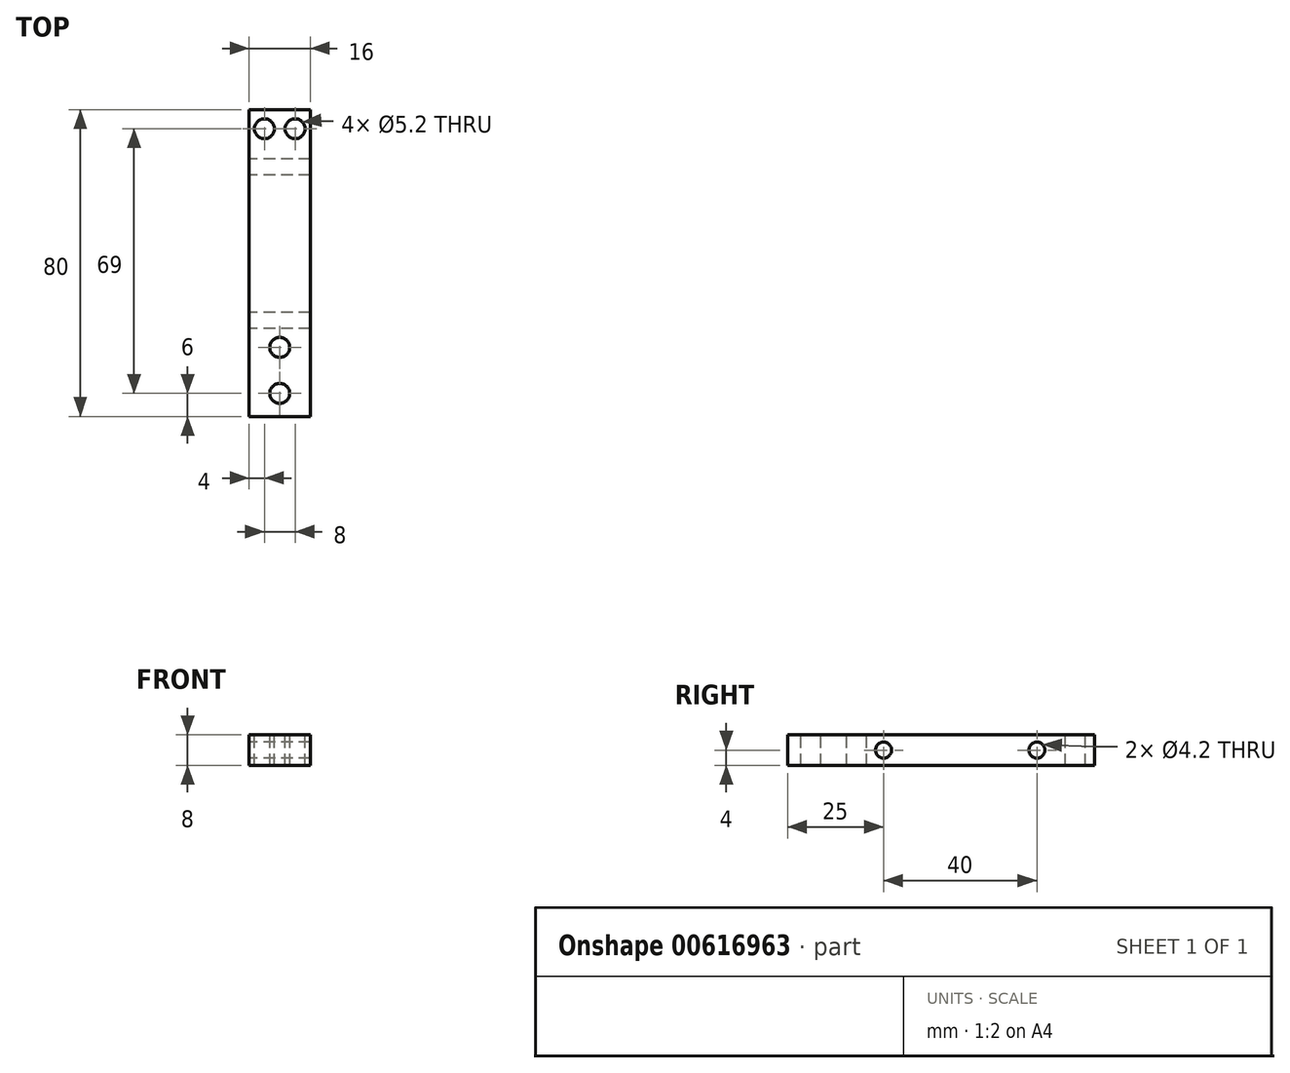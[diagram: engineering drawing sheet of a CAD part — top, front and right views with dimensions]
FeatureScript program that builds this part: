
annotation { "Feature Type Name" : "Feature", "Feature Type Description" : "" }
export const myFeature = defineFeature(function(context is Context, id is Id, definition is map)
    precondition{}
    {
        {
            var Q0;
            Q0=qCreatedBy(makeId("Front.planeOp"),FACE);
            var sketch = newSketch(context, id + "F0", { "sketchPlane" : qUnion([Q0])});
            skLineSegment(sketch, "E0.bottom", {"start": v(-8, 4) * mm, "end": v(8, 4) * mm});
            skLineSegment(sketch, "E0.top", {"start": v(-8, -4) * mm, "end": v(8, -4) * mm});
            skLineSegment(sketch, "E0.left", {"start": v(-8, 4) * mm, "end": v(-8, -4) * mm});
            skLineSegment(sketch, "E0.right", {"start": v(8, 4) * mm, "end": v(8, -4) * mm});
            skSolve(sketch);
        }
        {
            var Q0;
            Q0=makeQuery(id+"F0.imprint","IMPRINT",FACE,{"disambiguationData":[TD([[makeQuery(id+"F0.imprint","IMPRINT",EDGE,{"derivedFrom":sQuery(id+"F0.wireOp",EDGE,"E0.bottom")}),-1.0]])]});
            extrude(context, id + "F1", {"entities" : qUnion([Q0]), "oppositeDirection" : true, "depth" : 80 * mm, "offsetDistance" : 25 * mm});
        }
        {
            var Q0;
            Q0=makeQuery(id+"F1.opExtrude","SWEPT_FACE",FACE,{"disambiguationData":[OSD([sQuery(id+"F0.wireOp",EDGE,"E0.bottom")])]});
            var sketch = newSketch(context, id + "F2", { "sketchPlane" : qUnion([Q0])});
            skPoint(sketch, "E1", {"position": v(0, 6) * mm});
            skPoint(sketch, "E2", {"position": v(0, 18) * mm});
            skPoint(sketch, "E3", {"position": v(-4, 75) * mm});
            skPoint(sketch, "E4", {"position": v(4, 75) * mm});
            skCircle(sketch, "E5", {"center": v(-4, 75) * mm, "radius": 2.6 * mm});
            skCircle(sketch, "E6", {"center": v(4, 75) * mm, "radius": 2.6 * mm});
            skCircle(sketch, "E7", {"center": v(0, 18) * mm, "radius": 2.6 * mm});
            skCircle(sketch, "E8", {"center": v(0, 6) * mm, "radius": 2.6 * mm});
            skSolve(sketch);
        }
        {
            var Q0;
            Q0=makeQuery(id+"F1.opExtrude","SWEPT_FACE",FACE,{"disambiguationData":[OSD([sQuery(id+"F0.wireOp",EDGE,"E0.left")])]});
            var sketch = newSketch(context, id + "F3", { "sketchPlane" : qUnion([Q0])});
            skPoint(sketch, "E9", {"position": v(-25, 0) * mm});
            skPoint(sketch, "E10", {"position": v(-65, 0) * mm});
            skSolve(sketch);
        }
        {
            var Q0;
            Q0=makeQuery(id+"F2.imprint","IMPRINT",FACE,{"disambiguationData":[TD([[makeQuery(id+"F2.imprint","IMPRINT",EDGE,{"derivedFrom":sQuery(id+"F2.wireOp",EDGE,"E7")}),1.0]])]});
            var Q1;
            Q1=makeQuery(id+"F2.imprint","IMPRINT",FACE,{"disambiguationData":[TD([[makeQuery(id+"F2.imprint","IMPRINT",EDGE,{"derivedFrom":sQuery(id+"F2.wireOp",EDGE,"E8")}),1.0]])]});
            var Q2;
            Q2=makeQuery(id+"F2.imprint","IMPRINT",FACE,{"disambiguationData":[TD([[makeQuery(id+"F2.imprint","IMPRINT",EDGE,{"derivedFrom":sQuery(id+"F2.wireOp",EDGE,"E6")}),1.0]])]});
            var Q3;
            Q3=makeQuery(id+"F2.imprint","IMPRINT",FACE,{"disambiguationData":[TD([[makeQuery(id+"F2.imprint","IMPRINT",EDGE,{"derivedFrom":sQuery(id+"F2.wireOp",EDGE,"E5")}),1.0]])]});
            var Q4;
            Q4=sQuery(id+"F2.wireOp",EDGE,"E7");
            extrude(context, id + "F4", {"entities" : qUnion([Q0, Q1, Q2, Q3]), "operationType" : NewBodyOperationType.REMOVE, "surfaceEntities" : qUnion([Q4]), "oppositeDirection" : true, "depth" : 25 * mm, "offsetDistance" : 25 * mm, "hasSecondDirection" : true, "secondDirectionOppositeDirection" : false, "secondDirectionDepth" : 25 * mm});
        }
        {
            var Q0;
            Q0=sQuery(id+"F3.wireOp",VERTEX,"E10");
            var Q1;
            Q1=sQuery(id+"F3.wireOp",VERTEX,"E9");
            var Q2;
            Q2=makeQuery(id+"F1.opExtrude","SWEPT_BODY",BODY,{"disambiguationData":[OSD([sQuery(id+"F0.wireOp",EDGE,"E0.bottom"),sQuery(id+"F0.wireOp",EDGE,"E0.top"),sQuery(id+"F0.wireOp",EDGE,"E0.left"),sQuery(id+"F0.wireOp",EDGE,"E0.right")])]});
            hole(context, id + "F5", {"style" : HoleStyle.SIMPLE, "endStyle" : HoleEndStyle.BLIND, "standardTappedOrClearance" : lookupTablePath({ "standard" : "ISO", "engagement" : "75%", "pitch" : "0.8 mm", "size" : "M5", "type" : "Tapped" }), "standardBlindInLast" : lookupTablePath({ "standard" : "ISO", "engagement" : "75%", "pitch" : "0.8 mm", "size" : "M5", "type" : "Tapped" }), "holeDiameter" : 4.2 * mm, "majorDiameter" : 5 * mm, "showTappedDepth" : true, "holeDepth" : 18.4 * mm, "isTappedThrough" : true, "tappedDepth" : 16 * mm, "tapClearance" : 3, "locations" : qUnion([Q0, Q1]), "scope" : qUnion([Q2])});
        }
    });
